# Revit family: Fi_Attentes_EU_EC_EF
name_source: partatom
category: Appareils sanitaires
revit_build: Autodesk Revit 2017 (Build: 20160225_1515(x64)
units: mm (PartAtom-declared; Revit-internal decimal feet)

## family parameters
Basée sur le plan de construction = Non
Cote de connecteur circulaire = Utiliser le rayon
Couper avec des vides une fois chargée = Non
Partagée = Non
Point de calcul de pièce = Non
Toujours verticalement = Oui
Type d'élément = Normal

## types (7) — shared parameters
Connexion EC = Oui
Connexion EF = Oui
Eaux usagées = Oui
EntreAxe EC/EF = 100 mm  [stored 0.328084 ft]
Ventilation = Oui
Visibilite EC = Oui
Visibilite EF = Oui
Visibilite EU = Oui
zero-valued in all types: EntreAxe EU/EC, Hauteur EC-EF, Hauteur EU-EV

## per-type parameters (varying)
| type | DN EF_EC | DN EU | DTU_EC | DTU_EF | DTU_EU | RN EF-EC | RN EU |
| Bac a laver | 14 mm  [stored 0.0459318 ft] | 40 mm  [stored 0.131234 ft] | 0.3 L/s | 0.3 L/s | 0.8 L/s | 7 mm  [stored 0.0229659 ft] | 20 mm  [stored 0.0656168 ft] |
| Evier | 12 mm  [stored 0.0393701 ft] | 40 mm  [stored 0.131234 ft] | 0.2 L/s | 0.2 L/s | 0.8 L/s | 6 mm  [stored 0.019685 ft] | 20 mm  [stored 0.0656168 ft] |
| Lave Mains | 10 mm  [stored 0.0328084 ft] | 40 mm  [stored 0.131234 ft] | 0.3 L/s | 0.3 L/s | 0.5 L/s | 5 mm  [stored 0.0164042 ft] | 20 mm  [stored 0.0656168 ft] |
| Bidet | 10 mm  [stored 0.0328084 ft] | 40 mm  [stored 0.131234 ft] | 0.2 L/s | 0.2 L/s | 0.5 L/s | 5 mm  [stored 0.0164042 ft] | 20 mm  [stored 0.0656168 ft] |
| Lavabo | 10 mm  [stored 0.0328084 ft] | 40 mm  [stored 0.131234 ft] | 0.2 L/s | 0.2 L/s | 0.8 L/s | 5 mm  [stored 0.0164042 ft] | 20 mm  [stored 0.0656168 ft] |
| Douche | 10 mm  [stored 0.0328084 ft] | 40 mm  [stored 0.131234 ft] | 0.2 L/s | 0.2 L/s | 0.5 L/s | 5 mm  [stored 0.0164042 ft] | 20 mm  [stored 0.0656168 ft] |
| Baignoire | 14 mm  [stored 0.0459318 ft] | 50 mm  [stored 0.164042 ft] | 0.3 L/s | 0.3 L/s | 1.2 L/s | 7 mm  [stored 0.0229659 ft] | 25 mm  [stored 0.082021 ft] |

note: [stored X ft] marks values corroborated as IEEE doubles in the binary element streams (Revit-internal decimal feet)
